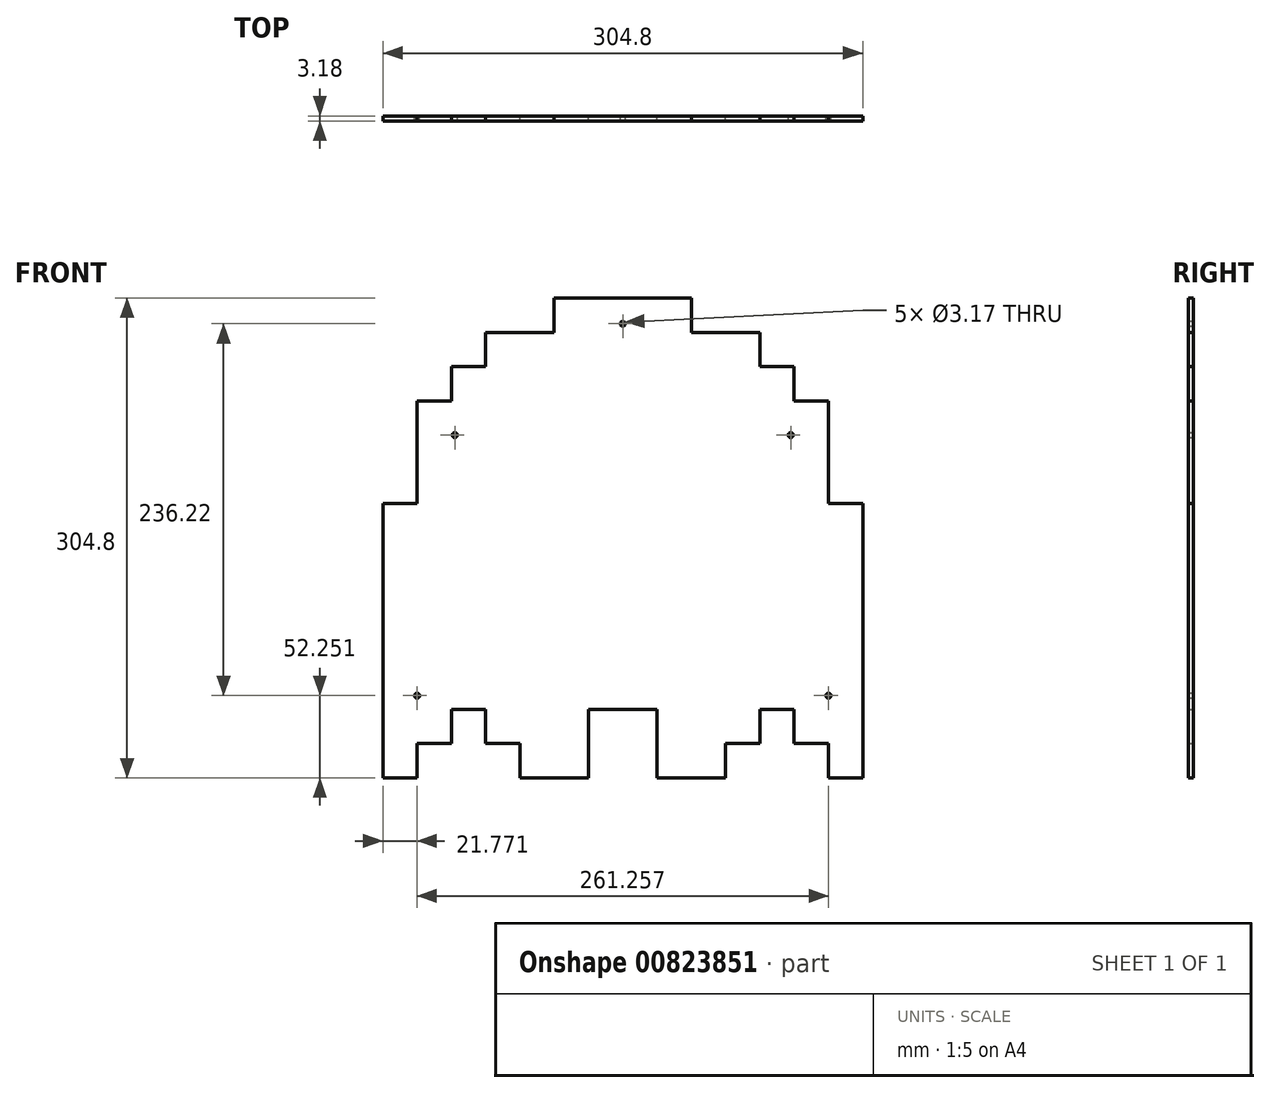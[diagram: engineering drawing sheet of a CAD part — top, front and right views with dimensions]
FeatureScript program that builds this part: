
annotation { "Feature Type Name" : "Feature", "Feature Type Description" : "" }
export const myFeature = defineFeature(function(context is Context, id is Id, definition is map)
    precondition{}
    {
        {
            var Q0;
            Q0=qCreatedBy(makeId("Front.planeOp"),FACE);
            var sketch = newSketch(context, id + "F0", { "sketchPlane" : qUnion([Q0])});
            skLineSegment(sketch, "E0", {"start": v(0, 0) * mm, "end": v(0, 174.17) * mm});
            skLineSegment(sketch, "E1", {"start": v(0, 174.17) * mm, "end": v(21.77, 174.17) * mm});
            skLineSegment(sketch, "E2", {"start": v(21.77, 174.17) * mm, "end": v(21.77, 239.49) * mm});
            skLineSegment(sketch, "E3", {"start": v(21.77, 239.49) * mm, "end": v(43.54, 239.49) * mm});
            skLineSegment(sketch, "E4", {"start": v(43.54, 239.49) * mm, "end": v(43.54, 261.26) * mm});
            skLineSegment(sketch, "E5", {"start": v(43.54, 261.26) * mm, "end": v(65.31, 261.26) * mm});
            skLineSegment(sketch, "E6", {"start": v(65.31, 261.26) * mm, "end": v(65.31, 283.03) * mm});
            skLineSegment(sketch, "E7", {"start": v(239.49, 283.03) * mm, "end": v(239.49, 261.26) * mm});
            skLineSegment(sketch, "E8", {"start": v(239.49, 261.26) * mm, "end": v(261.26, 261.26) * mm});
            skLineSegment(sketch, "E9", {"start": v(261.26, 261.26) * mm, "end": v(261.26, 239.49) * mm});
            skLineSegment(sketch, "E10", {"start": v(261.26, 239.49) * mm, "end": v(283.03, 239.49) * mm});
            skLineSegment(sketch, "E11", {"start": v(283.03, 239.49) * mm, "end": v(283.03, 174.17) * mm});
            skLineSegment(sketch, "E12", {"start": v(283.03, 174.17) * mm, "end": v(304.8, 174.17) * mm});
            skLineSegment(sketch, "E13", {"start": v(304.8, 174.17) * mm, "end": v(304.8, 0) * mm});
            skLineSegment(sketch, "E14", {"start": v(65.31, 283.03) * mm, "end": v(108.86, 283.03) * mm});
            skLineSegment(sketch, "E15", {"start": v(108.86, 283.03) * mm, "end": v(108.86, 304.8) * mm});
            skLineSegment(sketch, "E16", {"start": v(108.86, 304.8) * mm, "end": v(195.94, 304.8) * mm});
            skLineSegment(sketch, "E17", {"start": v(195.94, 304.8) * mm, "end": v(195.94, 283.03) * mm});
            skLineSegment(sketch, "E18", {"start": v(195.94, 283.03) * mm, "end": v(239.49, 283.03) * mm});
            skLineSegment(sketch, "E19", {"start": v(0, 0) * mm, "end": v(21.77, 0) * mm});
            skLineSegment(sketch, "E20", {"start": v(21.77, 0) * mm, "end": v(21.77, 21.77) * mm});
            skLineSegment(sketch, "E21", {"start": v(21.77, 21.77) * mm, "end": v(43.54, 21.77) * mm});
            skLineSegment(sketch, "E22", {"start": v(43.54, 21.77) * mm, "end": v(43.54, 43.54) * mm});
            skLineSegment(sketch, "E23", {"start": v(43.54, 43.54) * mm, "end": v(65.31, 43.54) * mm});
            skLineSegment(sketch, "E24", {"start": v(65.31, 43.54) * mm, "end": v(65.31, 21.77) * mm});
            skLineSegment(sketch, "E25", {"start": v(65.31, 21.77) * mm, "end": v(87.09, 21.77) * mm});
            skLineSegment(sketch, "E26", {"start": v(87.09, 21.77) * mm, "end": v(87.09, 0) * mm});
            skLineSegment(sketch, "E27", {"start": v(87.09, 0) * mm, "end": v(130.63, 0) * mm});
            skLineSegment(sketch, "E28", {"start": v(130.63, 0) * mm, "end": v(130.63, 43.54) * mm});
            skLineSegment(sketch, "E29", {"start": v(130.63, 43.54) * mm, "end": v(174.17, 43.54) * mm});
            skLineSegment(sketch, "E30", {"start": v(174.17, 43.54) * mm, "end": v(174.17, 0) * mm});
            skLineSegment(sketch, "E31", {"start": v(174.17, 0) * mm, "end": v(217.71, 0) * mm});
            skLineSegment(sketch, "E32", {"start": v(217.71, 0) * mm, "end": v(217.71, 21.77) * mm});
            skLineSegment(sketch, "E33", {"start": v(217.71, 21.77) * mm, "end": v(239.49, 21.77) * mm});
            skLineSegment(sketch, "E34", {"start": v(239.49, 21.77) * mm, "end": v(239.49, 43.54) * mm});
            skLineSegment(sketch, "E35", {"start": v(239.49, 43.54) * mm, "end": v(261.26, 43.54) * mm});
            skLineSegment(sketch, "E36", {"start": v(261.26, 43.54) * mm, "end": v(261.26, 21.77) * mm});
            skLineSegment(sketch, "E37", {"start": v(261.26, 21.77) * mm, "end": v(283.03, 21.77) * mm});
            skLineSegment(sketch, "E38", {"start": v(283.03, 21.77) * mm, "end": v(283.03, 0) * mm});
            skLineSegment(sketch, "E39", {"start": v(283.03, 0) * mm, "end": v(304.8, 0) * mm});
            skCircle(sketch, "E40", {"center": v(45.72, 217.71) * mm, "radius": 1.59 * mm});
            skCircle(sketch, "E41", {"center": v(259.08, 217.71) * mm, "radius": 1.59 * mm});
            skCircle(sketch, "E42", {"center": v(152.4, 288.47) * mm, "radius": 1.59 * mm});
            skCircle(sketch, "E43", {"center": v(21.77, 52.25) * mm, "radius": 1.59 * mm});
            skCircle(sketch, "E44", {"center": v(283.03, 52.25) * mm, "radius": 1.59 * mm});
            skSolve(sketch);
        }
        {
            var Q0;
            Q0=makeQuery(id+"F0.imprint","IMPRINT",FACE,{"disambiguationData":[TD([[makeQuery(id+"F0.imprint","IMPRINT",EDGE,{"derivedFrom":sQuery(id+"F0.wireOp",EDGE,"E0")}),-1.0]])]});
            extrude(context, id + "F1", {"entities" : qUnion([Q0]), "depth" : 3.17 * mm, "offsetDistance" : 25.4 * mm});
        }
    });
